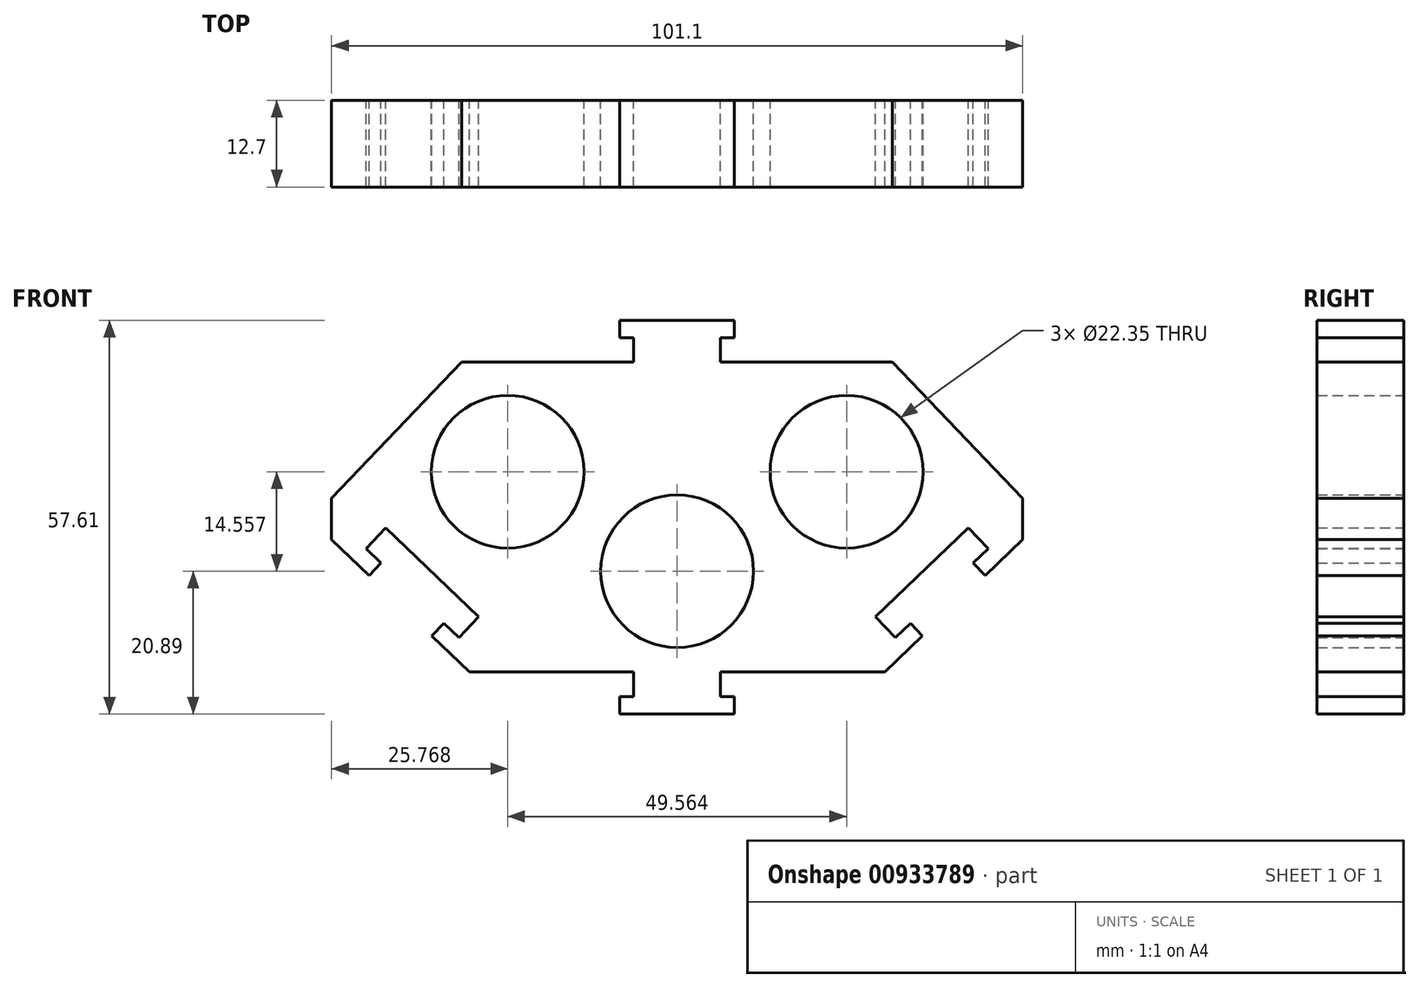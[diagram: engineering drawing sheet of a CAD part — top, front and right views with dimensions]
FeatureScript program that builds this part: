
annotation { "Feature Type Name" : "Feature", "Feature Type Description" : "" }
export const myFeature = defineFeature(function(context is Context, id is Id, definition is map)
    precondition{}
    {
        {
            var Q0;
            Q0=qCreatedBy(makeId("Front.planeOp"),FACE);
            var sketch = newSketch(context, id + "F0", { "sketchPlane" : qUnion([Q0])});
            skLineSegment(sketch, "E0", {"start": v(-8.38, 36.72) * mm, "end": v(0, 36.72) * mm});
            skLineSegment(sketch, "E1", {"start": v(-6.34, 33.59) * mm, "end": v(-6.34, 30.61) * mm});
            skLineSegment(sketch, "E2", {"start": v(-6.34, 30.61) * mm, "end": v(-31.5, 30.61) * mm});
            skLineSegment(sketch, "E3", {"start": v(-31.5, 30.61) * mm, "end": v(-50.55, 10.7) * mm});
            skLineSegment(sketch, "E4", {"start": v(-50.55, 10.7) * mm, "end": v(-50.55, 4.62) * mm});
            skLineSegment(sketch, "E5", {"start": v(-50.55, 4.62) * mm, "end": v(-45.05, -0.64) * mm});
            skLineSegment(sketch, "E6", {"start": v(-45.05, -0.64) * mm, "end": v(-43.3, 1.18) * mm});
            skLineSegment(sketch, "E7", {"start": v(-42.43, 6.14) * mm, "end": v(-35.82, -0.18) * mm});
            skLineSegment(sketch, "E8", {"start": v(-35.88, -9.44) * mm, "end": v(-30.37, -14.7) * mm});
            skLineSegment(sketch, "E9", {"start": v(0, -20.9) * mm, "end": v(0, 36.72) * mm, "construction": true});
            skCircle(sketch, "E10", {"center": v(0, 0) * mm, "radius": 11.18 * mm});
            skCircle(sketch, "E11.MirrorC", {"center": v(-24.78, 14.56) * mm, "radius": 11.18 * mm});
            skLineSegment(sketch, "E12", {"start": v(-8.38, 34.17) * mm, "end": v(-6.34, 34.17) * mm});
            skLineSegment(sketch, "E13", {"start": v(-6.34, 34.17) * mm, "end": v(-6.34, 33.59) * mm});
            skLineSegment(sketch, "E14", {"start": v(0, 36.72) * mm, "end": v(-8.38, 36.72) * mm});
            skLineSegment(sketch, "E15", {"start": v(-8.38, 36.72) * mm, "end": v(-8.38, 34.17) * mm});
            skLineSegment(sketch, "E16", {"start": v(-30.37, -14.7) * mm, "end": v(-6.34, -14.7) * mm});
            skLineSegment(sketch, "E17", {"start": v(0, -14.7) * mm, "end": v(0, 36.72) * mm});
            skLineSegment(sketch, "E18", {"start": v(-35.82, -0.18) * mm, "end": v(-42.62, 6.32) * mm});
            skLineSegment(sketch, "E19", {"start": v(-42.62, 6.32) * mm, "end": v(-44.9, 3.94) * mm});
            skLineSegment(sketch, "E20", {"start": v(-44.9, 3.94) * mm, "end": v(-45.51, 3.3) * mm});
            skLineSegment(sketch, "E21", {"start": v(-45.51, 3.3) * mm, "end": v(-43.3, 1.18) * mm});
            skPoint(sketch, "E22.start.orphan", {"position": v(-29.2, -6.5) * mm});
            skLineSegment(sketch, "E23.MirrorCS", {"start": v(-35.82, -0.18) * mm, "end": v(-29.02, -6.68) * mm});
            skLineSegment(sketch, "E24.MirrorCS", {"start": v(-29.02, -6.68) * mm, "end": v(-31.3, -9.06) * mm});
            skLineSegment(sketch, "E25.MirrorCS", {"start": v(-31.3, -9.06) * mm, "end": v(-31.92, -9.71) * mm});
            skLineSegment(sketch, "E26.MirrorCS", {"start": v(-31.92, -9.71) * mm, "end": v(-34.12, -7.6) * mm});
            skLineSegment(sketch, "E27.MirrorCS", {"start": v(-35.87, -9.42) * mm, "end": v(-34.12, -7.6) * mm});
            skLineSegment(sketch, "E28.MirrorCS", {"start": v(8.38, 34.17) * mm, "end": v(6.34, 34.17) * mm});
            skLineSegment(sketch, "E29.MirrorCS", {"start": v(6.34, 34.17) * mm, "end": v(6.34, 33.59) * mm});
            skLineSegment(sketch, "E30.MirrorCS", {"start": v(45.51, 3.3) * mm, "end": v(43.3, 1.18) * mm});
            skLineSegment(sketch, "E31.MirrorCS", {"start": v(31.3, -9.06) * mm, "end": v(31.92, -9.71) * mm});
            skLineSegment(sketch, "E32.MirrorCS", {"start": v(42.62, 6.32) * mm, "end": v(44.9, 3.94) * mm});
            skLineSegment(sketch, "E33.MirrorCS", {"start": v(45.05, -0.64) * mm, "end": v(43.3, 1.18) * mm});
            skLineSegment(sketch, "E34.MirrorCS", {"start": v(44.9, 3.94) * mm, "end": v(45.51, 3.3) * mm});
            skLineSegment(sketch, "E35.MirrorCS", {"start": v(31.92, -9.71) * mm, "end": v(34.12, -7.6) * mm});
            skLineSegment(sketch, "E36.MirrorCS", {"start": v(8.38, 36.72) * mm, "end": v(8.38, 34.17) * mm});
            skLineSegment(sketch, "E37.MirrorCS", {"start": v(29.02, -6.68) * mm, "end": v(31.3, -9.06) * mm});
            skLineSegment(sketch, "E38.MirrorCS", {"start": v(6.34, 33.59) * mm, "end": v(6.34, 30.61) * mm});
            skLineSegment(sketch, "E39.MirrorCS", {"start": v(35.87, -9.42) * mm, "end": v(34.12, -7.6) * mm});
            skLineSegment(sketch, "E40.MirrorCS", {"start": v(42.43, 6.14) * mm, "end": v(35.82, -0.18) * mm});
            skLineSegment(sketch, "E41.MirrorCS", {"start": v(8.38, 36.72) * mm, "end": v(0, 36.72) * mm});
            skLineSegment(sketch, "E42.MirrorCS", {"start": v(50.55, 10.7) * mm, "end": v(50.55, 4.62) * mm});
            skLineSegment(sketch, "E43.MirrorCS", {"start": v(30.37, -14.7) * mm, "end": v(6.34, -14.7) * mm});
            skLineSegment(sketch, "E44.MirrorCS", {"start": v(31.5, 30.61) * mm, "end": v(50.55, 10.7) * mm});
            skLineSegment(sketch, "E45.MirrorCS", {"start": v(50.55, 4.62) * mm, "end": v(45.05, -0.64) * mm});
            skLineSegment(sketch, "E46.MirrorCS", {"start": v(35.82, -0.18) * mm, "end": v(29.02, -6.68) * mm});
            skCircle(sketch, "E47.MirrorC", {"center": v(24.78, 14.56) * mm, "radius": 11.18 * mm});
            skPoint(sketch, "E48.MirrorP", {"position": v(29.2, -6.5) * mm});
            skLineSegment(sketch, "E49.MirrorCS", {"start": v(35.82, -0.18) * mm, "end": v(42.62, 6.32) * mm});
            skLineSegment(sketch, "E50.MirrorCS", {"start": v(35.88, -9.44) * mm, "end": v(30.37, -14.7) * mm});
            skLineSegment(sketch, "E51.MirrorCS", {"start": v(6.34, 30.61) * mm, "end": v(31.5, 30.61) * mm});
            skLineSegment(sketch, "E52.MirrorCS", {"start": v(0, 36.72) * mm, "end": v(8.38, 36.72) * mm});
            skLineSegment(sketch, "E53", {"start": v(8.38, 36.72) * mm, "end": v(-8.38, 36.72) * mm});
            skLineSegment(sketch, "E54", {"start": v(-43.3, 1.18) * mm, "end": v(-45.51, 3.3) * mm});
            skLineSegment(sketch, "E55", {"start": v(-45.51, 3.3) * mm, "end": v(-42.62, 6.32) * mm});
            skLineSegment(sketch, "E56", {"start": v(-42.62, 6.32) * mm, "end": v(-29.02, -6.68) * mm});
            skLineSegment(sketch, "E57", {"start": v(-29.02, -6.68) * mm, "end": v(-31.92, -9.71) * mm});
            skLineSegment(sketch, "E58", {"start": v(-34.12, -7.6) * mm, "end": v(-35.88, -9.44) * mm});
            skLineSegment(sketch, "E59", {"start": v(30.37, -14.7) * mm, "end": v(35.88, -9.44) * mm});
            skLineSegment(sketch, "E60", {"start": v(35.88, -9.44) * mm, "end": v(34.12, -7.6) * mm});
            skLineSegment(sketch, "E61", {"start": v(8.38, -20.9) * mm, "end": v(0, -20.9) * mm});
            skLineSegment(sketch, "E62", {"start": v(6.34, -17.76) * mm, "end": v(6.34, -14.78) * mm});
            skLineSegment(sketch, "E63", {"start": v(8.38, -18.34) * mm, "end": v(6.34, -18.34) * mm});
            skLineSegment(sketch, "E64", {"start": v(6.34, -18.34) * mm, "end": v(6.34, -17.76) * mm});
            skLineSegment(sketch, "E65", {"start": v(0, -20.9) * mm, "end": v(8.38, -20.9) * mm});
            skLineSegment(sketch, "E66", {"start": v(8.38, -20.9) * mm, "end": v(8.38, -18.34) * mm});
            skLineSegment(sketch, "E67.MirrorCS", {"start": v(-8.38, -18.34) * mm, "end": v(-6.34, -18.34) * mm});
            skLineSegment(sketch, "E68.MirrorCS", {"start": v(-6.34, -18.34) * mm, "end": v(-6.34, -17.76) * mm});
            skLineSegment(sketch, "E69.MirrorCS", {"start": v(-8.38, -20.9) * mm, "end": v(-8.38, -18.34) * mm});
            skLineSegment(sketch, "E70.MirrorCS", {"start": v(-6.34, -17.76) * mm, "end": v(-6.34, -14.78) * mm});
            skLineSegment(sketch, "E71.MirrorCS", {"start": v(-8.38, -20.9) * mm, "end": v(0, -20.9) * mm});
            skLineSegment(sketch, "E72.MirrorCS", {"start": v(0, -20.9) * mm, "end": v(-8.38, -20.9) * mm});
            skLineSegment(sketch, "E73", {"start": v(-8.38, -20.9) * mm, "end": v(8.38, -20.9) * mm});
            skLineSegment(sketch, "E74", {"start": v(-6.34, -14.78) * mm, "end": v(-6.34, -14.7) * mm});
            skLineSegment(sketch, "E75", {"start": v(6.34, -14.78) * mm, "end": v(6.34, -14.7) * mm});
            skPoint(sketch, "E76.orphan", {"position": v(0, -14.7) * mm});
            skLineSegment(sketch, "E77.trimOffspring", {"start": v(6.34, -14.7) * mm, "end": v(30.37, -14.7) * mm});
            skSolve(sketch);
        }
        {
            var Q0;
            Q0=makeQuery(id+"F0.imprint","IMPRINT",FACE,{"disambiguationData":[TD([[makeQuery(id+"F0.imprint","IMPRINT",EDGE,{"derivedFrom":sQuery(id+"F0.wireOp",EDGE,"E1")}),1.0]])]});
            var Q1;
            Q1=makeQuery(id+"F0.imprint","IMPRINT",FACE,{"disambiguationData":[TD([[makeQuery(id+"F0.imprint","IMPRINT",EDGE,{"derivedFrom":sQuery(id+"F0.wireOp",EDGE,"E28.MirrorCS")}),-1.0]])]});
            extrude(context, id + "F1", {"entities" : qUnion([Q0, Q1]), "depth" : 12.7 * mm, "offsetDistance" : 25.4 * mm});
        }
    });
